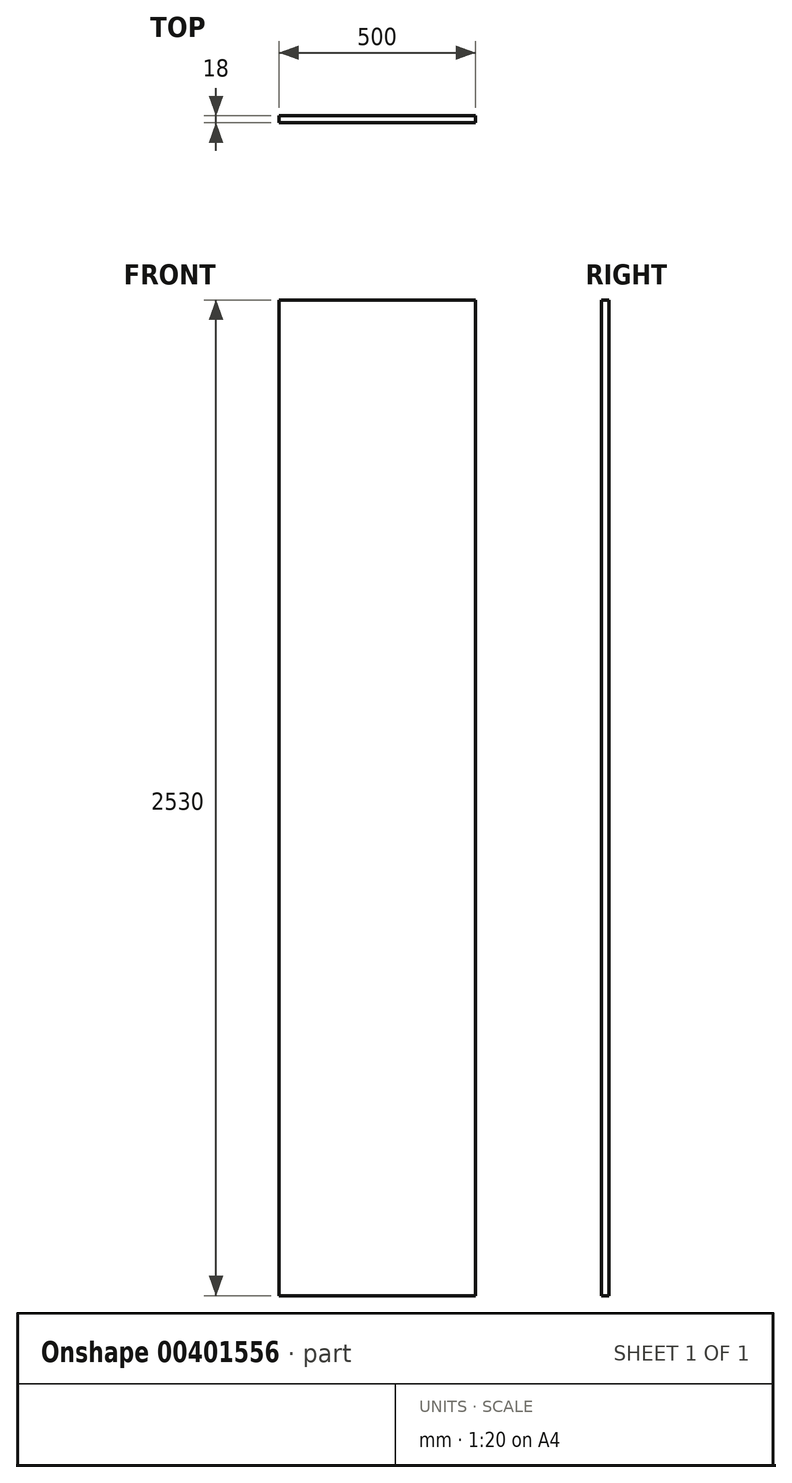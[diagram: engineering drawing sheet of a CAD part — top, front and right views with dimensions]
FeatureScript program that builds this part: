
annotation { "Feature Type Name" : "Feature", "Feature Type Description" : "" }
export const myFeature = defineFeature(function(context is Context, id is Id, definition is map)
    precondition{}
    {
        {
            var Q0;
            Q0=qCreatedBy(makeId("Front.planeOp"),FACE);
            var sketch = newSketch(context, id + "F0", { "sketchPlane" : qUnion([Q0])});
            skLineSegment(sketch, "E0.bottom", {"start": v(-1159.28, 1309.63) * mm, "end": v(-659.28, 1309.63) * mm});
            skLineSegment(sketch, "E0.top", {"start": v(-1159.28, -1220.37) * mm, "end": v(-659.28, -1220.37) * mm});
            skLineSegment(sketch, "E0.left", {"start": v(-1159.28, 1309.63) * mm, "end": v(-1159.28, -1220.37) * mm});
            skLineSegment(sketch, "E0.right", {"start": v(-659.28, 1309.63) * mm, "end": v(-659.28, -1220.37) * mm});
            skSolve(sketch);
        }
        {
            var Q0;
            Q0 = qSketchRegion(id + "F0", true);
            extrude(context, id + "F1", {"entities" : qUnion([Q0]), "depth" : 18 * mm});
        }
    });
